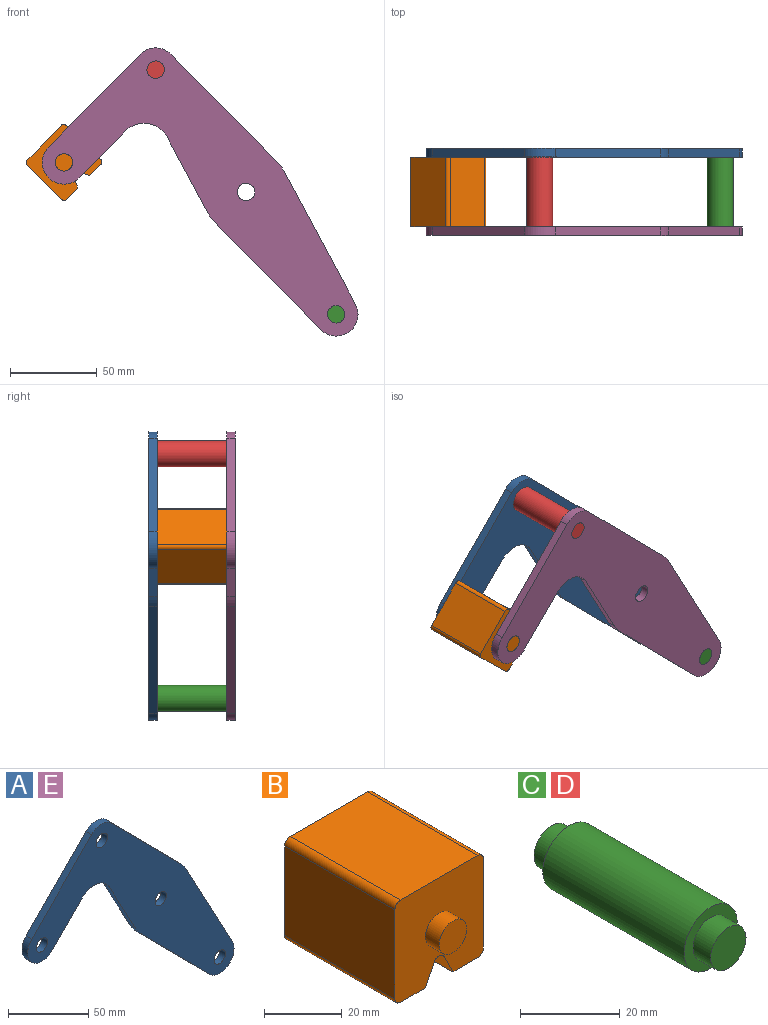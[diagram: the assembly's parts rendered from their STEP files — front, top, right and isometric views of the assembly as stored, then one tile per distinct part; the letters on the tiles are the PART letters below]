
ASSEMBLY  parts=5 mates=3
PART A: 18 faces, bbox 181.7x5x165.8 mm
  f0: plane 43.49x23.35mm, normal (-0.88,0,-0.47), area 246.8mm2, adj f1,f14,f16,f17
  f1: cylinder r=25mm len=5.75mm, axis (0,1,0), area 35.8mm2, adj f0,f2,f16,f17
  f2: plane 61.6x60.87mm, normal (-0.71,0,-0.7), area 433mm2, adj f1,f3,f16,f17
  f3: cylinder r=12.5mm len=21.39mm, axis (0,1,0), area 178.4mm2, adj f2,f4,f16,f17
  f4: plane 76.3x40.96mm, normal (0.88,0,0.47), area 433mm2, adj f3,f5,f16,f17
  f5: cylinder r=25mm len=5.75mm, axis (0,1,0), area 35.8mm2, adj f4,f6,f16,f17
  f6: plane 61.6x60.87mm, normal (0.71,0,0.7), area 433mm2, adj f5,f7,f16,f17
  f7: cylinder r=12.5mm len=17.78mm, axis (0,1,0), area 98.9mm2, adj f6,f8,f16,f17
  f8: plane 53.35x52.71mm, normal (-0.71,0,0.7), area 375mm2, adj f7,f9,f16,f17
  f9: cylinder r=12.5mm len=21.39mm, axis (0,1,0), area 196.3mm2, adj f8,f10,f16,f17
  f10: plane 26.86x26.54mm, normal (0.71,0,-0.7), area 188.8mm2, adj f9,f14,f16,f17
  f11: cylinder r=5mm len=10mm, axis (0,1,0), area 157.1mm2, adj f16,f17
  f12: cylinder r=5mm len=10mm, axis (0,1,0), area 157.1mm2, adj f16,f17
  f13: cylinder r=5mm len=10mm, axis (0,1,0), area 157.1mm2, adj f16,f17
  f14: cylinder r=15mm len=23.89mm, axis (0,1,0), area 140.2mm2, adj f0,f10,f16,f17
  f15: cylinder r=5mm len=10mm, axis (0,1,0), area 157.1mm2, adj f16,f17
  f16: plane 181.66x165.78mm, normal (0,-1,0), area 8710.1mm2, adj f0,f1,f2,f3,f4,f5,f6,f7
  f17: plane 181.66x165.78mm, normal (0,1,0), area 8710.1mm2, adj f0,f1,f2,f3,f4,f5,f6,f7
PART B: 18 faces, bbox 32.1x50x32.1 mm
  f0: plane 40x28.08mm, normal (1,0,0), area 1123.1mm2, adj f4,f10,f13,f14
  f1: plane 40x9.04mm, normal (0,0,-1), area 361.6mm2, adj f2,f4,f10,f14
  f2: plane 40x6.42mm, normal (-0.89,0,-0.45), area 287.2mm2, adj f1,f4,f10,f15
  f3: plane 40x6.42mm, normal (0.89,0,-0.45), area 287.2mm2, adj f4,f5,f10,f15
  f4: plane 32.08x32.08mm, normal (0,-1,0), area 900.6mm2, adj f0,f1,f2,f3,f5,f6,f7,f9
  f5: plane 40x9.04mm, normal (0,0,-1), area 361.6mm2, adj f3,f4,f10,f16
  f6: plane 40x28.08mm, normal (0,0,1), area 1123.1mm2, adj f4,f10,f13,f17
  f7: plane 40x28.08mm, normal (-1,0,0), area 1123.1mm2, adj f4,f10,f16,f17
  f8: plane 10x10mm, normal (0,-1,0), area 78.5mm2, adj f9
  f9: cylinder r=5mm len=10mm, axis (0,1,0), area 157.1mm2, adj f4,f8
  f10: plane 32.08x32.08mm, normal (0,1,0), area 900.6mm2, adj f0,f1,f2,f3,f5,f6,f7,f12
  f11: plane 10x10mm, normal (0,1,0), area 78.5mm2, adj f12
  f12: cylinder r=5mm len=10mm, axis (0,-1,0), area 157.1mm2, adj f10,f11
  f13: cylinder r=2mm len=40mm, axis (0,1,0), area 125.7mm2, adj f0,f4,f6,f10
  f14: cylinder r=2mm len=40mm, axis (0,-1,0), area 125.7mm2, adj f0,f1,f4,f10
  f15: cylinder r=2mm len=40mm, axis (0,1,0), area 177.1mm2, adj f2,f3,f4,f10
  f16: cylinder r=2mm len=40mm, axis (0,1,0), area 125.7mm2, adj f4,f5,f7,f10
  f17: cylinder r=2mm len=40mm, axis (0,-1,0), area 125.7mm2, adj f4,f6,f7,f10
PART C: 7 faces, bbox 15x50x15 mm
  f0: cylinder r=7.5mm len=40mm, axis (0,-1,0), area 1885mm2, adj f2,f5
  f1: cylinder r=5mm len=10mm, axis (0,1,0), area 157.1mm2, adj f2,f3
  f2: plane 15x15mm, normal (0,-1,0), area 98.2mm2, adj f0,f1
  f3: plane 10x10mm, normal (0,-1,0), area 78.5mm2, adj f1
  f4: cylinder r=5mm len=10mm, axis (0,-1,0), area 157.1mm2, adj f5,f6
  f5: plane 15x15mm, normal (0,1,0), area 98.2mm2, adj f0,f4
  f6: plane 10x10mm, normal (0,1,0), area 78.5mm2, adj f4
PART D: same geometry as C
PART E: same geometry as A
PLACE A t=(0,50,0)mm
PLACE B rot(axis=(0,-1,0),45.6deg) t=(-19.32,5,79.98)mm
PLACE C t=(103.95,5,-140.78)mm
PLACE D t=(0,5,0)mm
PLACE E t=(0,5,0)mm fixed
MATE revolute E.f9 <-> B.f9  axis (0,1,0) through (-104.69,5,17.04)mm
MATE fastened D.f0 <-> A.f7  axis (0,-1,0) through (-51.98,45,70.39)mm
MATE fastened E.f3 <-> C.f0  axis (0,1,0) through (51.98,5,-70.39)mm
